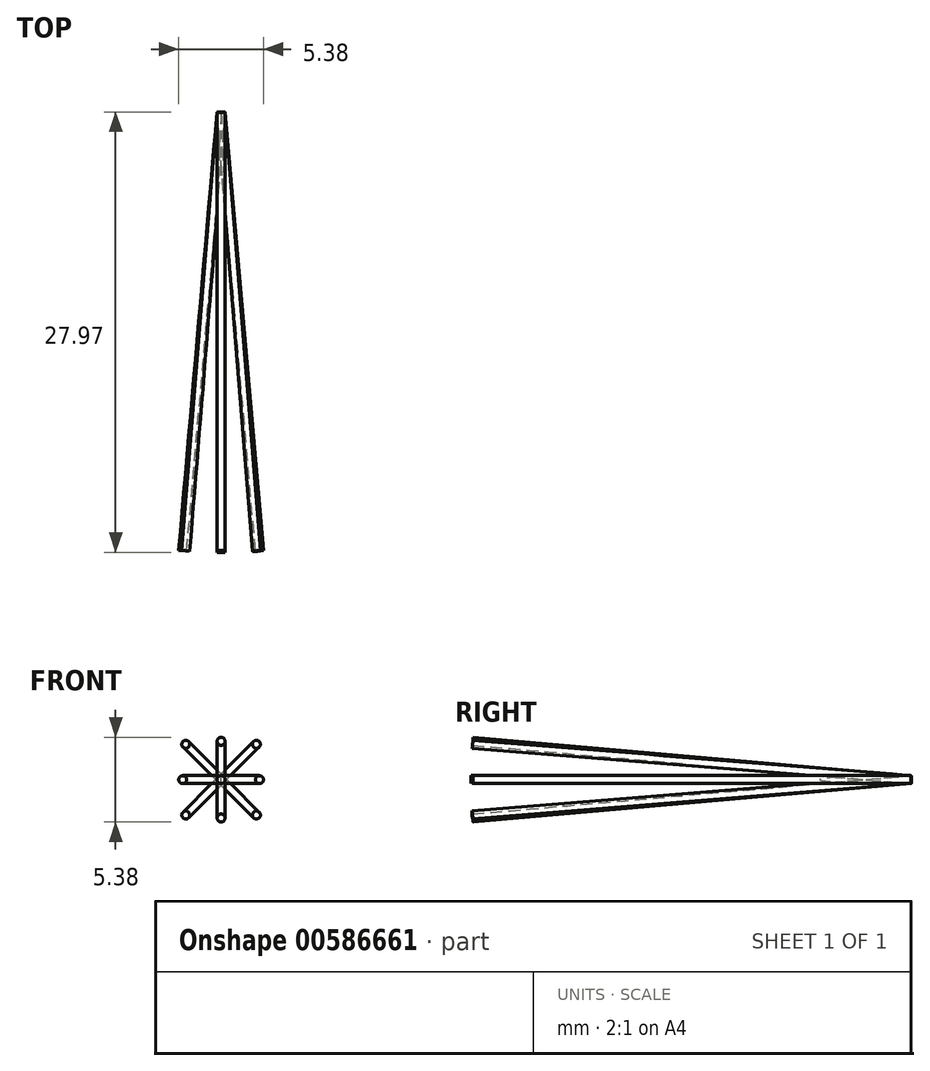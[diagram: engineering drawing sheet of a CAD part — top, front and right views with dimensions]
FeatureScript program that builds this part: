
annotation { "Feature Type Name" : "Feature", "Feature Type Description" : "" }
export const myFeature = defineFeature(function(context is Context, id is Id, definition is map)
    precondition{}
    {
        {
            var Q0;
            Q0=qCreatedBy(makeId("Front.planeOp"),FACE);
            var sketch = newSketch(context, id + "F0", { "sketchPlane" : qUnion([Q0])});
            skCircle(sketch, "E0", {"center": v(0, 0) * mm, "radius": 0.25 * mm});
            skSolve(sketch);
        }
        {
            var Q0;
            Q0=makeQuery(id+"F0.imprint","IMPRINT",FACE,{"disambiguationData":[TD([[makeQuery(id+"F0.imprint","IMPRINT",EDGE,{"derivedFrom":sQuery(id+"F0.wireOp",EDGE,"E0")}),1.0]])]});
            extrude(context, id + "F1", {"entities" : qUnion([Q0]), "depth" : 27.94 * mm, "offsetDistance" : 25.4 * mm});
        }
        {
            var Q0;
            Q0=qCreatedBy(makeId("Front.planeOp"),FACE);
            var sketch = newSketch(context, id + "F2", { "sketchPlane" : qUnion([Q0])});
            skLineSegment(sketch, "E1", {"start": v(0, 34.55) * mm, "end": v(0, 22.2) * mm});
            skSolve(sketch);
        }
        {
            var Q0;
            Q0=qCreatedBy(makeId("Front.planeOp"),FACE);
            var Q1;
            Q1=sQuery(id+"F2.wireOp",EDGE,"E1");
            cPlane(context, id + "F3", {"entities" : qUnion([Q0, Q1]), "cplaneType" : CPlaneType.LINE_ANGLE, "offset" : 25.4 * mm, "angle" : 5 * degree, "width" : 152.4 * mm, "height" : 152.4 * mm});
        }
        {
            var Q0;
            Q0=qCreatedBy(id+"F3.planeOp",FACE);
            var sketch = newSketch(context, id + "F4", { "sketchPlane" : qUnion([Q0])});
            skCircle(sketch, "E2", {"center": v(0, 0) * mm, "radius": 0.25 * mm});
            skSolve(sketch);
        }
        {
            var Q0;
            Q0 = qSketchRegion(id + "F4", true);
            extrude(context, id + "F5", {"entities" : qUnion([Q0]), "operationType" : NewBodyOperationType.ADD, "oppositeDirection" : true, "depth" : 27.94 * mm, "offsetDistance" : 25.4 * mm});
        }
        {
            var Q0;
            Q0=qCreatedBy(makeId("Front.planeOp"),FACE);
            var Q1;
            Q1=sQuery(id+"F2.wireOp",EDGE,"E1");
            cPlane(context, id + "F6", {"entities" : qUnion([Q0, Q1]), "cplaneType" : CPlaneType.LINE_ANGLE, "offset" : 25.4 * mm, "angle" : 175 * degree, "width" : 152.4 * mm, "height" : 152.4 * mm});
        }
        {
            var Q0;
            Q0=qCreatedBy(id+"F6.planeOp",FACE);
            var sketch = newSketch(context, id + "F7", { "sketchPlane" : qUnion([Q0])});
            skCircle(sketch, "E3", {"center": v(0, 0) * mm, "radius": 0.25 * mm});
            skSolve(sketch);
        }
        {
            var Q0;
            Q0 = qSketchRegion(id + "F7", true);
            extrude(context, id + "F8", {"entities" : qUnion([Q0]), "operationType" : NewBodyOperationType.ADD, "depth" : 27.94 * mm, "offsetDistance" : 25.4 * mm});
        }
        {
            var Q0;
            Q0=qCreatedBy(makeId("Front.planeOp"),FACE);
            var sketch = newSketch(context, id + "F9", { "sketchPlane" : qUnion([Q0])});
            skLineSegment(sketch, "E4", {"start": v(0, 0) * mm, "end": v(58.72, 0) * mm});
            skSolve(sketch);
        }
        {
            var Q0;
            Q0=sQuery(id+"F9.wireOp",EDGE,"E4");
            cPlane(context, id + "F10", {"entities" : qUnion([Q0]), "cplaneType" : CPlaneType.LINE_ANGLE, "offset" : 25.4 * mm, "angle" : 5 * degree, "width" : 152.4 * mm, "height" : 152.4 * mm});
        }
        {
            var Q0;
            Q0=qCreatedBy(id+"F10.planeOp",FACE);
            var sketch = newSketch(context, id + "F11", { "sketchPlane" : qUnion([Q0])});
            skCircle(sketch, "E5", {"center": v(0, 0) * mm, "radius": 0.25 * mm});
            skSolve(sketch);
        }
        {
            var Q0;
            Q0 = qSketchRegion(id + "F11", true);
            extrude(context, id + "F12", {"entities" : qUnion([Q0]), "oppositeDirection" : true, "depth" : 27.94 * mm, "offsetDistance" : 25.4 * mm});
        }
        {
            var Q0;
            Q0=qCreatedBy(makeId("Front.planeOp"),FACE);
            var Q1;
            Q1=sQuery(id+"F9.wireOp",EDGE,"E4");
            cPlane(context, id + "F13", {"entities" : qUnion([Q0, Q1]), "cplaneType" : CPlaneType.LINE_ANGLE, "offset" : 25.4 * mm, "angle" : 175 * degree, "width" : 152.4 * mm, "height" : 152.4 * mm});
        }
        {
            var Q0;
            Q0=qCreatedBy(id+"F13.planeOp",FACE);
            var sketch = newSketch(context, id + "F14", { "sketchPlane" : qUnion([Q0])});
            skCircle(sketch, "E6", {"center": v(0, 0) * mm, "radius": 0.25 * mm});
            skSolve(sketch);
        }
        {
            var Q0;
            Q0 = qSketchRegion(id + "F14", true);
            extrude(context, id + "F15", {"entities" : qUnion([Q0]), "depth" : 27.94 * mm, "offsetDistance" : 25.4 * mm});
        }
        {
            var Q0;
            Q0=qCreatedBy(makeId("Front.planeOp"),FACE);
            var sketch = newSketch(context, id + "F16", { "sketchPlane" : qUnion([Q0])});
            skLineSegment(sketch, "E7", {"start": v(0, 0) * mm, "end": v(31.57, 31.57) * mm});
            skLineSegment(sketch, "E8", {"start": v(0, 0) * mm, "end": v(-26.93, 26.93) * mm});
            skSolve(sketch);
        }
        {
            var Q0;
            Q0=qCreatedBy(makeId("Front.planeOp"),FACE);
            var Q1;
            Q1=sQuery(id+"F16.wireOp",EDGE,"E7");
            cPlane(context, id + "F17", {"entities" : qUnion([Q0, Q1]), "cplaneType" : CPlaneType.LINE_ANGLE, "offset" : 25.4 * mm, "angle" : 6.5 * degree, "width" : 152.4 * mm, "height" : 152.4 * mm});
        }
        {
            var Q0;
            Q0=qCreatedBy(id+"F17.planeOp",FACE);
            var sketch = newSketch(context, id + "F18", { "sketchPlane" : qUnion([Q0])});
            skCircle(sketch, "E9", {"center": v(0, 0) * mm, "radius": 0.25 * mm});
            skSolve(sketch);
        }
        {
            var Q0;
            Q0 = qSketchRegion(id + "F18", true);
            extrude(context, id + "F19", {"entities" : qUnion([Q0]), "oppositeDirection" : true, "depth" : 28.04 * mm, "offsetDistance" : 25.4 * mm});
        }
        {
            var Q0;
            Q0=qCreatedBy(makeId("Front.planeOp"),FACE);
            var Q1;
            Q1=sQuery(id+"F16.wireOp",EDGE,"E7");
            cPlane(context, id + "F20", {"entities" : qUnion([Q0, Q1]), "cplaneType" : CPlaneType.LINE_ANGLE, "offset" : 25.4 * mm, "angle" : 173.5 * degree, "width" : 152.4 * mm, "height" : 152.4 * mm});
        }
        {
            var Q0;
            Q0=qCreatedBy(id+"F20.planeOp",FACE);
            var sketch = newSketch(context, id + "F21", { "sketchPlane" : qUnion([Q0])});
            skCircle(sketch, "E10", {"center": v(0, 0) * mm, "radius": 0.25 * mm});
            skSolve(sketch);
        }
        {
            var Q0;
            Q0 = qSketchRegion(id + "F21", true);
            extrude(context, id + "F22", {"entities" : qUnion([Q0]), "depth" : 28.04 * mm, "offsetDistance" : 25.4 * mm});
        }
        {
            var Q0;
            Q0=qCreatedBy(makeId("Front.planeOp"),FACE);
            var Q1;
            Q1=sQuery(id+"F16.wireOp",EDGE,"E8");
            cPlane(context, id + "F23", {"entities" : qUnion([Q0, Q1]), "cplaneType" : CPlaneType.LINE_ANGLE, "offset" : 25.4 * mm, "angle" : 6.5 * degree, "width" : 152.4 * mm, "height" : 152.4 * mm});
        }
        {
            var Q0;
            Q0=qCreatedBy(id+"F23.planeOp",FACE);
            var sketch = newSketch(context, id + "F24", { "sketchPlane" : qUnion([Q0])});
            skCircle(sketch, "E11", {"center": v(0, 0) * mm, "radius": 0.25 * mm});
            skSolve(sketch);
        }
        {
            var Q0;
            Q0 = qSketchRegion(id + "F24", true);
            extrude(context, id + "F25", {"entities" : qUnion([Q0]), "oppositeDirection" : true, "depth" : 28.04 * mm, "offsetDistance" : 25.4 * mm});
        }
        {
            var Q0;
            Q0=qCreatedBy(makeId("Front.planeOp"),FACE);
            var Q1;
            Q1=sQuery(id+"F16.wireOp",EDGE,"E8");
            cPlane(context, id + "F26", {"entities" : qUnion([Q0, Q1]), "cplaneType" : CPlaneType.LINE_ANGLE, "offset" : 25.4 * mm, "angle" : 173.5 * degree, "width" : 152.4 * mm, "height" : 152.4 * mm});
        }
        {
            var Q0;
            Q0=qCreatedBy(id+"F26.planeOp",FACE);
            var sketch = newSketch(context, id + "F27", { "sketchPlane" : qUnion([Q0])});
            skCircle(sketch, "E12", {"center": v(0, 0) * mm, "radius": 0.25 * mm});
            skSolve(sketch);
        }
        {
            var Q0;
            Q0 = qSketchRegion(id + "F27", true);
            extrude(context, id + "F28", {"entities" : qUnion([Q0]), "depth" : 28.04 * mm, "offsetDistance" : 25.4 * mm});
        }
    });
